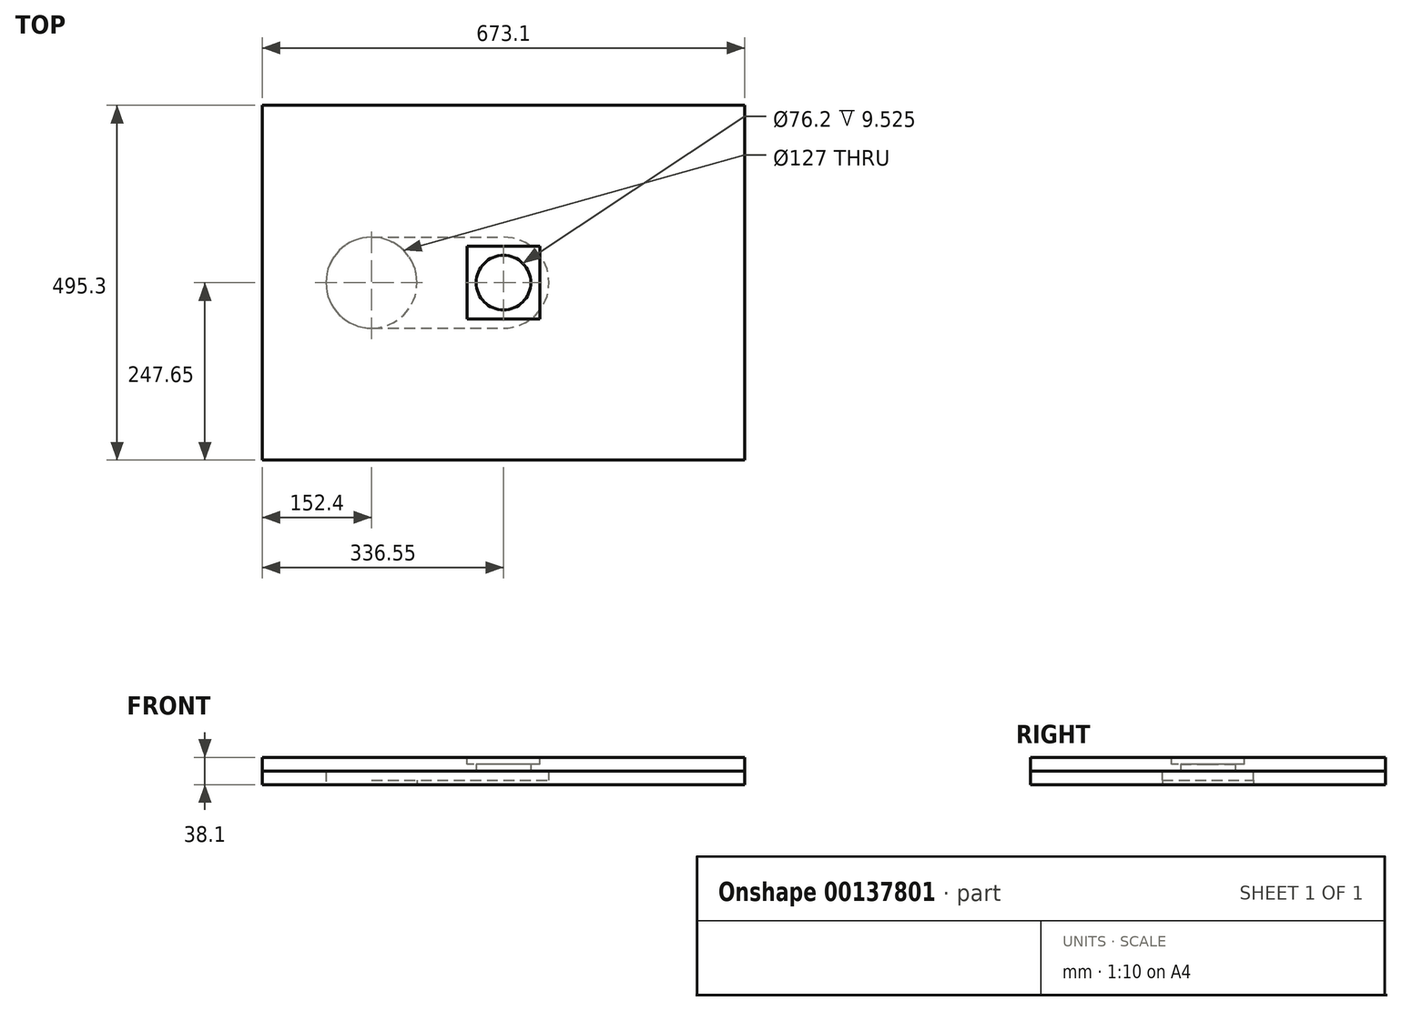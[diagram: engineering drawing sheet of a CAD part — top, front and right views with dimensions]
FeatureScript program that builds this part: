
annotation { "Feature Type Name" : "Feature", "Feature Type Description" : "" }
export const myFeature = defineFeature(function(context is Context, id is Id, definition is map)
    precondition{}
    {
        {
            var Q0;
            Q0=qCreatedBy(makeId("Top.planeOp"),FACE);
            var sketch = newSketch(context, id + "F0", { "sketchPlane" : qUnion([Q0])});
            skLineSegment(sketch, "E0.bottom", {"start": v(336.55, 247.65) * mm, "end": v(-336.55, 247.65) * mm});
            skLineSegment(sketch, "E0.top", {"start": v(336.55, -247.65) * mm, "end": v(-336.55, -247.65) * mm});
            skLineSegment(sketch, "E0.left", {"start": v(336.55, 247.65) * mm, "end": v(336.55, -247.65) * mm});
            skLineSegment(sketch, "E0.right", {"start": v(-336.55, 247.65) * mm, "end": v(-336.55, -247.65) * mm});
            skPoint(sketch, "E0.middle", {"position": v(0, 0) * mm});
            skLineSegment(sketch, "E1", {"start": v(-336.55, 247.65) * mm, "end": v(-336.55, 285.75) * mm, "construction": true});
            skLineSegment(sketch, "E2", {"start": v(-336.55, 285.75) * mm, "end": v(336.55, 285.75) * mm, "construction": true});
            skLineSegment(sketch, "E3", {"start": v(336.55, 285.75) * mm, "end": v(336.55, 247.65) * mm, "construction": true});
            skLineSegment(sketch, "E4", {"start": v(-298.45, 247.65) * mm, "end": v(-298.45, -247.65) * mm, "construction": true});
            skLineSegment(sketch, "E5", {"start": v(-69.85, 247.65) * mm, "end": v(-69.85, -247.65) * mm, "construction": true});
            skCircle(sketch, "E6", {"center": v(-184.15, 0) * mm, "radius": 63.5 * mm});
            skSolve(sketch);
        }
        {
            var Q0;
            Q0 = qSketchRegion(id + "F0", true);
            extrude(context, id + "F1", {"entities" : qUnion([Q0]), "depth" : 19.05 * mm});
        }
        {
            var Q0;
            Q0=makeQuery(id+"F1.opExtrude","CAP_FACE",FACE,{"disambiguationData":[OSD([sQuery(id+"F0.wireOp",EDGE,"E0.bottom"),sQuery(id+"F0.wireOp",EDGE,"E0.top"),sQuery(id+"F0.wireOp",EDGE,"E0.left"),sQuery(id+"F0.wireOp",EDGE,"E0.right"),sQuery(id+"F0.wireOp",EDGE,"E6")])],"isStart":false});
            var sketch = newSketch(context, id + "F2", { "sketchPlane" : qUnion([Q0])});
            skArc(sketch, "E7", {"start": v(0, -63.5) * mm, "mid": v(63.5, 0) * mm, "end": v(0, 63.5) * mm});
            skArc(sketch, "E8.0", {"start": v(-184.15, 63.5) * mm, "mid": v(-247.65, 0) * mm, "end": v(-184.15, -63.5) * mm});
            skLineSegment(sketch, "E9", {"start": v(-184.15, 63.5) * mm, "end": v(0, 63.5) * mm});
            skLineSegment(sketch, "E10", {"start": v(-184.15, -63.5) * mm, "end": v(0, -63.5) * mm});
            skSolve(sketch);
        }
        {
            var Q0;
            Q0 = qSketchRegion(id + "F2", true);
            extrude(context, id + "F3", {"entities" : qUnion([Q0]), "operationType" : NewBodyOperationType.REMOVE, "oppositeDirection" : true, "depth" : 12.7 * mm});
        }
        {
            var Q0;
            Q0=makeQuery(id+"F1.opExtrude","CAP_FACE",FACE,{"disambiguationData":[OSD([sQuery(id+"F0.wireOp",EDGE,"E0.bottom"),sQuery(id+"F0.wireOp",EDGE,"E0.top"),sQuery(id+"F0.wireOp",EDGE,"E0.left"),sQuery(id+"F0.wireOp",EDGE,"E0.right"),sQuery(id+"F0.wireOp",EDGE,"E6")])],"isStart":false});
            var sketch = newSketch(context, id + "F4", { "sketchPlane" : qUnion([Q0])});
            skLineSegment(sketch, "E11.0", {"start": v(336.55, 247.65) * mm, "end": v(-336.55, 247.65) * mm});
            skLineSegment(sketch, "E12.0", {"start": v(-336.55, 247.65) * mm, "end": v(-336.55, -247.65) * mm});
            skLineSegment(sketch, "E13.0", {"start": v(336.55, -247.65) * mm, "end": v(-336.55, -247.65) * mm});
            skLineSegment(sketch, "E14.0", {"start": v(336.55, 247.65) * mm, "end": v(336.55, -247.65) * mm});
            skPoint(sketch, "E15.0", {"position": v(0, 0) * mm});
            skCircle(sketch, "E16", {"center": v(0, 0) * mm, "radius": 38.1 * mm});
            skSolve(sketch);
        }
        {
            var Q0;
            Q0 = qSketchRegion(id + "F4", true);
            extrude(context, id + "F5", {"entities" : qUnion([Q0]), "depth" : 19.05 * mm});
        }
        {
            var Q0;
            Q0=makeQuery(id+"F5.opExtrude","CAP_FACE",FACE,{"disambiguationData":[OSD([sQuery(id+"F4.wireOp",EDGE,"E11.0"),sQuery(id+"F4.wireOp",EDGE,"E12.0"),sQuery(id+"F4.wireOp",EDGE,"E13.0"),sQuery(id+"F4.wireOp",EDGE,"E14.0"),sQuery(id+"F4.wireOp",EDGE,"E16")])],"isStart":false});
            var sketch = newSketch(context, id + "F6", { "sketchPlane" : qUnion([Q0])});
            skPoint(sketch, "E17.0", {"position": v(0, 0) * mm});
            skLineSegment(sketch, "E18.bottom", {"start": v(50.8, 50.8) * mm, "end": v(-50.8, 50.8) * mm});
            skLineSegment(sketch, "E18.top", {"start": v(50.8, -50.8) * mm, "end": v(-50.8, -50.8) * mm});
            skLineSegment(sketch, "E18.left", {"start": v(50.8, 50.8) * mm, "end": v(50.8, -50.8) * mm});
            skLineSegment(sketch, "E18.right", {"start": v(-50.8, 50.8) * mm, "end": v(-50.8, -50.8) * mm});
            skSolve(sketch);
        }
        {
            var Q0;
            Q0 = qSketchRegion(id + "F6", true);
            extrude(context, id + "F7", {"entities" : qUnion([Q0]), "operationType" : NewBodyOperationType.REMOVE, "oppositeDirection" : true, "depth" : 9.52 * mm});
        }
    });
